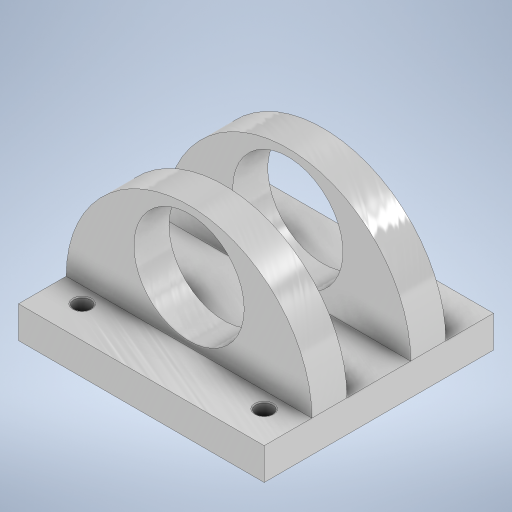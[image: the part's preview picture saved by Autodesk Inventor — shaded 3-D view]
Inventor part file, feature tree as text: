
AUTODESK INVENTOR PART (.ipt)
format: ipt  version: 2023 (Build 270158000, 158)  size: 335,872 bytes
history: native  units: in
note: dims shown in document units (in); Inventor stores cm internally (conversion verified against a paired STEP export)
features: sketch x5, extrude x3, plane x2, mirror x2, hole x1, fillet x1
ambient origin geometry x8: Origin, YZ Plane, XZ Plane, XY Plane, X Axis, Y Axis, Z Axis, Center Point
bodies: Solid1 (feature_tree)
feature tree (14):
  extrude  "Extrusion1"  Depth=1.8in
  sketch  "Sketch3"  dims[d2=0.25in d3=0.0in d4=0.5in d5=0.65in]
  hole  "Hole1"  [1 undecoded]
  fillet  "Fillet1"  Radius=0.65in
  plane  "Work Plane1"
  extrude  "Extrusion2"  Depth=0.25in
  plane  "Work Plane2"
  mirror  "Mirror1"
  extrude  "Extrusion3"  Depth=0.25in
  mirror  "Mirror2"
  sketch  "Sketch1"  dims[d0=1.929in d1=1.8in]
  sketch  "Sketch4"  dims[d6=0.242in d7=0.25in]
  sketch  "Sketch5"  dims[d8=0.25in d9=0.25in]
  sketch  "Sketch6"  dims[d10=0.25in d11=0.25in d12=0.25in d13=0.25in d14=0.25in d15=0.1339in d16=0.75in d17=0.256in d18=0.118in d19=90.0deg d20=0.3937in d21=0.8108in d22=0.0079in d23=-0.65in d24=0.2756in d25=0.0in d26=-0.9in d27=0.475in d28=0.8661in d29=1.0in d30=0.0in]
note: 1 required parameter value undecoded (feature->parameter linkage not recoverable at this tier; creation-order binding heuristic only, values carry confidence <= 0.55)
